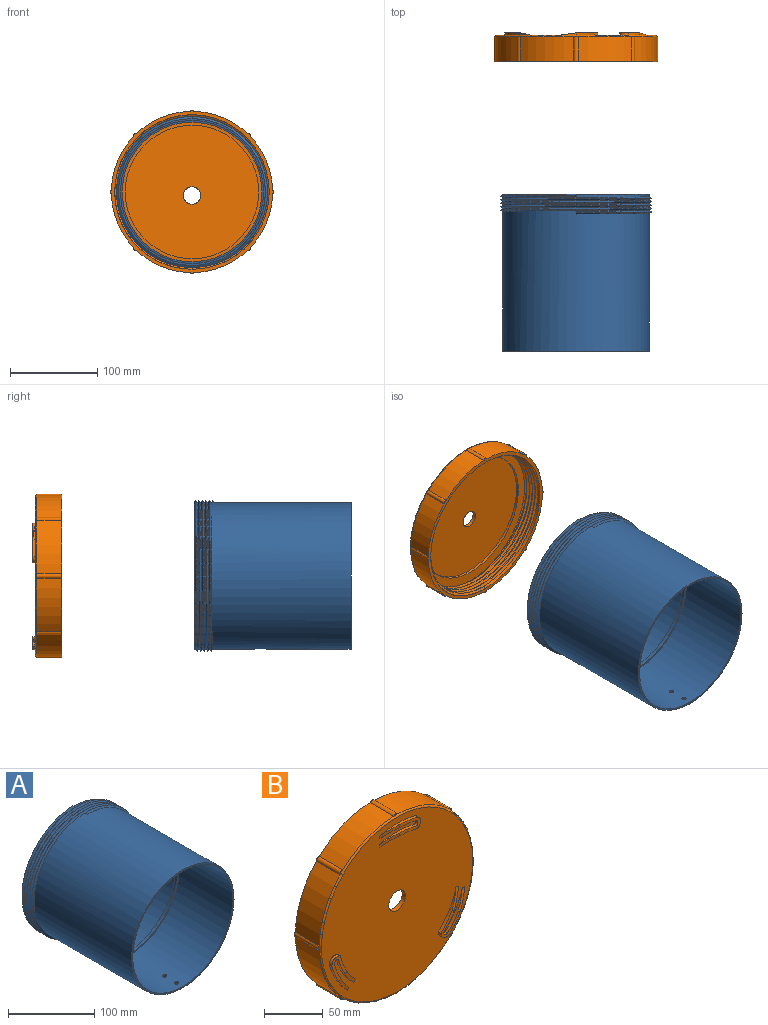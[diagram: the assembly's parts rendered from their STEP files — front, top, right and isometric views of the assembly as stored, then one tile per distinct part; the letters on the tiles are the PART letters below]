
ASSEMBLY  parts=2 mates=1
PART A: 20 faces, bbox 199.8x180x173 mm
  f0: cylinder r=84mm len=168mm, axis (0,1,0), area 83625.4mm2, adj f5,f8,f14,f15,f17,f18,f19
  f1: cylinder r=84mm len=168mm, axis (0,1,0), area 1055.6mm2, adj f2,f9,f13,f16
  f2: cylinder r=84mm len=168mm, axis (0,1,0), area 587.6mm2, adj f1,f3,f15,f16
  f3: cylinder r=84mm len=168mm, axis (0,1,0), area 587.6mm2, adj f2,f4,f15,f16
  f4: cylinder r=84mm len=168mm, axis (0,1,0), area 587.6mm2, adj f3,f5,f15,f16
  f5: cylinder r=84mm len=168mm, axis (0,1,0), area 587.6mm2, adj f0,f4,f15,f16
  f6: cylinder r=82mm len=164mm, axis (0,1,0), area 45300.5mm2, adj f8,f10,f18,f19
  f7: cylinder r=82mm len=164mm, axis (0,1,0), area 45025.2mm2, adj f9,f11,f17
  f8: plane 168x168mm, normal (0,-1,0), area 1043mm2, adj f0,f6
  f9: plane 168x168mm, normal (0,1,0), area 1043mm2, adj f1,f7
  f10: plane 164x164mm, normal (0,-1,0), area 1017.9mm2, adj f6,f12
  f11: plane 164x164mm, normal (0,1,0), area 1017.9mm2, adj f7,f12
  f12: cylinder r=80mm len=160mm, axis (0,1,0), area 2010.6mm2, adj f10,f11
  f13: plane 2.89x2.5mm, normal (1,0,0), area 3.6mm2, adj f1,f15,f16
  f14: plane 2.89x2.5mm, normal (-1,0,0), area 3.6mm2, adj f0,f15,f16
  f15: bspline ~199.76x173mm, area 7725.5mm2, adj f0,f2,f3,f4,f5,f13,f14,f16
  f16: bspline ~199.76x173mm, area 7731.3mm2, adj f1,f2,f3,f4,f5,f13,f14,f15
  f17: cylinder r=10mm len=20mm, axis (0,0,1), area 126.1mm2, adj f0,f7
  f18: cylinder r=2.5mm len=5mm, axis (0,0,1), area 31.4mm2, adj f0,f6
  f19: cylinder r=2.5mm len=5mm, axis (0,0,1), area 31.4mm2, adj f0,f6
PART B: 74 faces, bbox 207x35.6x202.9 mm
  f0: plane 182.02x182.02mm, normal (0,-1,0), area 24838.9mm2, adj f14,f35,f36,f37,f40,f41,f42,f43
  f1: cylinder r=92.5mm len=61.25mm, axis (0,1,0), area 1932.3mm2, adj f10,f14,f30,f32
  f2: cylinder r=92.5mm len=61.25mm, axis (0,1,0), area 1932.3mm2, adj f10,f14,f18,f32
  f3: cylinder r=92.5mm len=61.25mm, axis (0,1,0), area 1932.3mm2, adj f10,f14,f28,f30
  f4: cylinder r=92.5mm len=61.25mm, axis (0,1,0), area 1932.3mm2, adj f10,f14,f26,f28
  f5: cylinder r=92.5mm len=61.25mm, axis (0,1,0), area 1932.3mm2, adj f10,f14,f24,f26
  f6: cylinder r=92.5mm len=61.25mm, axis (0,1,0), area 1932.3mm2, adj f10,f14,f22,f24
  f7: cylinder r=92.5mm len=61.25mm, axis (0,1,0), area 1932.3mm2, adj f10,f14,f20,f22
  f8: cylinder r=92.5mm len=61.25mm, axis (0,1,0), area 1932.3mm2, adj f10,f14,f18,f20
  f9: cylinder r=88.5mm len=177mm, axis (0,1,0), area 5330.2mm2, adj f10,f11,f15,f16,f17
  f10: plane 187.4x187.4mm, normal (0,1,0), area 2307.2mm2, adj f1,f2,f3,f4,f5,f6,f7,f8
  f11: plane 178.62x177.65mm, normal (0,1,0), area 5788.2mm2, adj f9,f12,f16,f17
  f12: cylinder r=76.5mm len=153mm, axis (0,1,0), area 1442mm2, adj f11,f13
  f13: plane 153x153mm, normal (0,1,0), area 18071.2mm2, adj f12,f73
  f14: torus R=91mm, axis (0,-1,0), area 1361.3mm2, adj f0,f1,f2,f3,f4,f5,f6,f7
  f15: plane 2.89x2.5mm, normal (1,0,0), area 3.6mm2, adj f9,f16,f17
  f16: bspline ~204.38x177mm, area 7672.4mm2, adj f9,f11,f15,f17
  f17: bspline ~204.38x177mm, area 7173.2mm2, adj f9,f11,f15,f16
  f18: cylinder r=3mm len=28.5mm, axis (0,1,0), area 161mm2, adj f2,f8,f10,f19
  f19: plane 4.85x1.23mm, normal (0,-1,0), area 4.1mm2, adj f14,f18
  f20: cylinder r=3mm len=28.5mm, axis (0,1,0), area 161mm2, adj f7,f8,f10,f21
  f21: plane 3.47x3.47mm, normal (0,-1,0), area 4.1mm2, adj f14,f20
  f22: cylinder r=3mm len=28.5mm, axis (0,1,0), area 161mm2, adj f6,f7,f10,f23
  f23: plane 4.85x1.23mm, normal (0,-1,0), area 4.1mm2, adj f14,f22
  f24: cylinder r=3mm len=28.5mm, axis (0,1,0), area 161mm2, adj f5,f6,f10,f25
  f25: plane 3.47x3.47mm, normal (0,-1,0), area 4.1mm2, adj f14,f24
  f26: cylinder r=3mm len=28.5mm, axis (0,1,0), area 161mm2, adj f4,f5,f10,f27
  f27: plane 4.85x1.23mm, normal (0,-1,0), area 4.1mm2, adj f14,f26
  f28: cylinder r=3mm len=28.5mm, axis (0,1,0), area 161mm2, adj f3,f4,f10,f29
  f29: plane 3.47x3.47mm, normal (0,-1,0), area 4.1mm2, adj f14,f28
  f30: cylinder r=3mm len=28.5mm, axis (0,1,0), area 161mm2, adj f1,f3,f10,f31
  f31: plane 4.85x1.23mm, normal (0,-1,0), area 4.1mm2, adj f14,f30
  f32: cylinder r=3mm len=28.5mm, axis (0,1,0), area 161mm2, adj f1,f2,f10,f33
  f33: plane 3.47x3.47mm, normal (0,-1,0), area 4.1mm2, adj f14,f32
  f34: plane 25.24x14.65mm, normal (0,-1,0), area 160mm2, adj f35,f36,f37,f38,f39,f40,f41,f42
  f35: cylinder r=84.5mm len=21.38mm, axis (0,-1,0), area 32.5mm2, adj f0,f34,f37,f44
  f36: cylinder r=81.5mm len=41.06mm, axis (0,-1,0), area 92.2mm2, adj f0,f34,f37,f38,f42
  f37: plane 21.4x5.68mm, normal (-0.13,-0.99,-0.04), area 64.3mm2, adj f0,f34,f35,f36,f38
  f38: plane 2.87x0.1mm, normal (-1,0,0), area 0.1mm2, adj f34,f36,f37
  f39: plane 2.73x0.11mm, normal (-1,0,0), area 0.1mm2, adj f34,f41,f46
  f40: cylinder r=76mm len=42.19mm, axis (0,-1,0), area 95.8mm2, adj f0,f34,f42,f46
  f41: bspline ~21.32x3.18mm, area 64.4mm2, adj f0,f34,f39,f43,f45
  f42: cylinder r=3.5mm len=5.79mm, axis (0,1,0), area 20.5mm2, adj f0,f34,f36,f40
  f43: bspline ~11.97x4.12mm, area 44.5mm2, adj f0,f34,f41,f44
  f44: bspline ~21.66x3mm, area 65.4mm2, adj f0,f34,f35,f43
  f45: cylinder r=73mm len=20.58mm, axis (0,-1,0), area 30.2mm2, adj f0,f41,f46
  f46: plane 21.45x5.99mm, normal (-0.13,-0.99,-0.04), area 64.5mm2, adj f0,f34,f39,f40,f45
  f47: plane 27.01x18.36mm, normal (0,-1,0), area 160mm2, adj f48,f49,f50,f51,f52,f53,f54,f55
  f48: cylinder r=84.5mm len=17.14mm, axis (0,-1,0), area 32.5mm2, adj f0,f47,f50,f57
  f49: cylinder r=81.5mm len=35.53mm, axis (0,-1,0), area 92.2mm2, adj f0,f47,f50,f51,f55
  f50: plane 18.67x15.21mm, normal (0.1,-0.99,-0.1), area 64.3mm2, adj f0,f47,f48,f49,f51
  f51: plane 2.48x1.43mm, normal (0.5,0,-0.87), area 0.1mm2, adj f47,f49,f50
  f52: plane 2.36x1.36mm, normal (0.5,0,-0.87), area 0.1mm2, adj f47,f54,f59
  f53: cylinder r=76mm len=36.44mm, axis (0,-1,0), area 95.8mm2, adj f0,f47,f55,f59
  f54: bspline ~20.05x7.91mm, area 64.4mm2, adj f0,f47,f52,f56,f58
  f55: cylinder r=3.5mm len=4.85mm, axis (0,1,0), area 20.5mm2, adj f0,f47,f49,f53
  f56: bspline ~10.59x7.03mm, area 44.5mm2, adj f0,f47,f54,f57
  f57: bspline ~20.17x8.39mm, area 65.4mm2, adj f0,f47,f48,f56
  f58: cylinder r=73mm len=16.34mm, axis (0,-1,0), area 30.2mm2, adj f0,f54,f59
  f59: plane 18.54x15.44mm, normal (0.1,-0.99,-0.1), area 64.5mm2, adj f0,f47,f52,f53,f58
  f60: plane 24.12x23.33mm, normal (0,-1,0), area 160mm2, adj f61,f62,f63,f64,f65,f66,f67,f68
  f61: cylinder r=84.5mm len=19.89mm, axis (0,-1,0), area 32.5mm2, adj f0,f60,f63,f70
  f62: cylinder r=81.5mm len=35.58mm, axis (0,-1,0), area 92.2mm2, adj f0,f60,f63,f64,f68
  f63: plane 20.68x10.93mm, normal (0.04,-0.99,0.13), area 64.3mm2, adj f0,f60,f61,f62,f64
  f64: plane 2.48x1.43mm, normal (0.5,0,0.87), area 0.1mm2, adj f60,f62,f63
  f65: plane 2.36x1.36mm, normal (0.5,0,0.87), area 0.1mm2, adj f60,f67,f72
  f66: cylinder r=76mm len=36.63mm, axis (0,-1,0), area 95.8mm2, adj f0,f60,f68,f72
  f67: bspline ~16.88x13.41mm, area 64.4mm2, adj f0,f60,f65,f69,f71
  f68: cylinder r=3.5mm len=5.18mm, axis (0,1,0), area 20.5mm2, adj f0,f60,f62,f66
  f69: bspline ~10.19x7.51mm, area 44.5mm2, adj f0,f60,f67,f70
  f70: bspline ~17.35x13.28mm, area 65.4mm2, adj f0,f60,f61,f69
  f71: cylinder r=73mm len=19.3mm, axis (0,-1,0), area 30.2mm2, adj f0,f67,f72
  f72: plane 20.76x10.67mm, normal (0.03,-0.99,0.14), area 64.5mm2, adj f0,f60,f65,f66,f71
  f73: cylinder r=10mm len=20mm, axis (0,-1,0), area 251.3mm2, adj f0,f13
PLACE A t=(77.73,89.39,-53.28)mm
PLACE B rot(axis=(1,0,0),180deg) t=(77.73,241.39,-53.28)mm
MATE fastened B.f1 <-> A.f0  axis (0,-1,0) through (77.73,264.39,-53.28)mm
